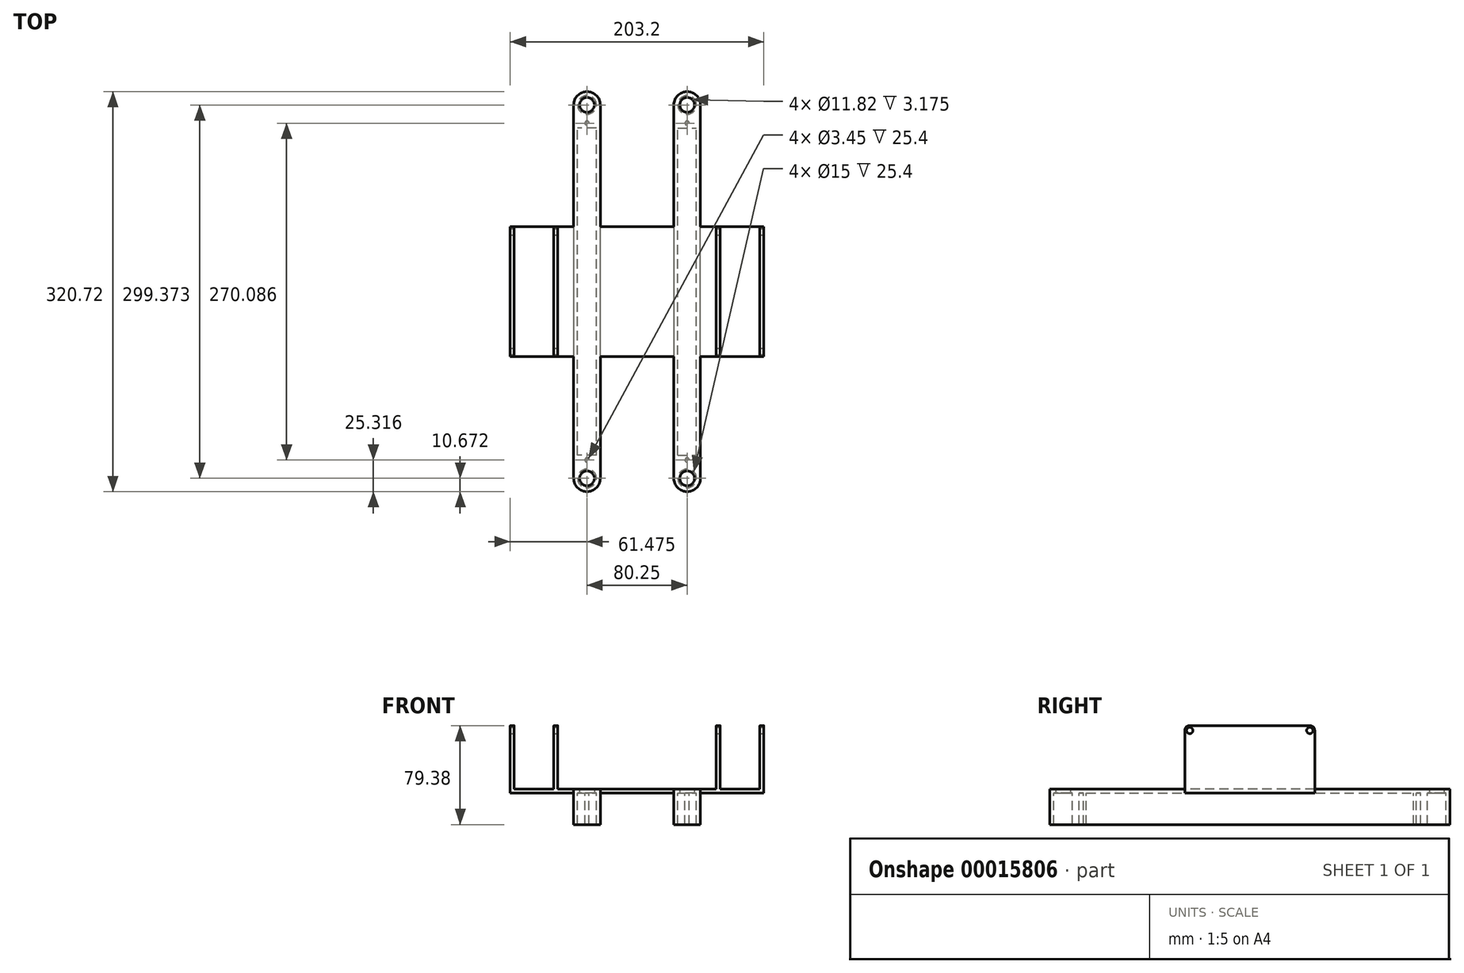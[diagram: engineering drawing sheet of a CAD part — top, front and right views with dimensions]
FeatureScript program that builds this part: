
annotation { "Feature Type Name" : "Feature", "Feature Type Description" : "" }
export const myFeature = defineFeature(function(context is Context, id is Id, definition is map)
    precondition{}
    {
        {
            var Q0;
            Q0=qCreatedBy(makeId("Top.planeOp"),FACE);
            var sketch = newSketch(context, id + "F0", { "sketchPlane" : qUnion([Q0])});
            skLineSegment(sketch, "E0.bottom", {"start": v(0, 0) * mm, "end": v(21.35, 0) * mm, "construction": true});
            skLineSegment(sketch, "E0.top", {"start": v(0, 97.64) * mm, "end": v(21.35, 97.64) * mm, "construction": true});
            skLineSegment(sketch, "E0.left", {"start": v(0, 0) * mm, "end": v(0, 97.64) * mm});
            skLineSegment(sketch, "E0.right", {"start": v(21.35, 0) * mm, "end": v(21.35, 97.64) * mm});
            skLineSegment(sketch, "E1.bottom", {"start": v(0, 0) * mm, "end": v(-50.8, 0) * mm});
            skLineSegment(sketch, "E1.top", {"start": v(0, -104.1) * mm, "end": v(-50.8, -104.1) * mm});
            skLineSegment(sketch, "E1.left", {"start": v(0, 0) * mm, "end": v(0, -104.1) * mm, "construction": true});
            skLineSegment(sketch, "E1.right", {"start": v(-50.8, 0) * mm, "end": v(-50.8, -104.1) * mm});
            skLineSegment(sketch, "E2.bottom", {"start": v(0, -104.1) * mm, "end": v(21.35, -104.1) * mm, "construction": true});
            skLineSegment(sketch, "E2.top", {"start": v(0, -201.74) * mm, "end": v(21.35, -201.74) * mm, "construction": true});
            skLineSegment(sketch, "E2.left", {"start": v(0, -104.1) * mm, "end": v(0, -201.74) * mm});
            skLineSegment(sketch, "E2.right", {"start": v(21.35, -104.1) * mm, "end": v(21.35, -201.74) * mm});
            skLineSegment(sketch, "E3.bottom", {"start": v(21.35, -104.1) * mm, "end": v(80.25, -104.1) * mm});
            skLineSegment(sketch, "E3.top", {"start": v(21.35, 0) * mm, "end": v(80.25, 0) * mm});
            skLineSegment(sketch, "E3.left", {"start": v(21.35, -104.1) * mm, "end": v(21.35, 0) * mm, "construction": true});
            skLineSegment(sketch, "E3.right", {"start": v(80.25, -104.1) * mm, "end": v(80.25, 0) * mm, "construction": true});
            skLineSegment(sketch, "E4.bottom", {"start": v(80.25, 0) * mm, "end": v(101.6, 0) * mm, "construction": true});
            skLineSegment(sketch, "E4.top", {"start": v(80.25, 97.64) * mm, "end": v(101.6, 97.64) * mm, "construction": true});
            skLineSegment(sketch, "E4.left", {"start": v(80.25, 0) * mm, "end": v(80.25, 97.64) * mm});
            skLineSegment(sketch, "E4.right", {"start": v(101.6, 0) * mm, "end": v(101.6, 97.64) * mm});
            skLineSegment(sketch, "E5.bottom", {"start": v(101.6, 0) * mm, "end": v(152.4, 0) * mm});
            skLineSegment(sketch, "E5.top", {"start": v(101.6, -104.1) * mm, "end": v(152.4, -104.1) * mm});
            skLineSegment(sketch, "E5.left", {"start": v(101.6, 0) * mm, "end": v(101.6, -104.1) * mm, "construction": true});
            skLineSegment(sketch, "E5.right", {"start": v(152.4, 0) * mm, "end": v(152.4, -104.1) * mm});
            skLineSegment(sketch, "E6.bottom", {"start": v(80.25, -104.1) * mm, "end": v(101.6, -104.1) * mm, "construction": true});
            skLineSegment(sketch, "E6.top", {"start": v(80.25, -201.74) * mm, "end": v(101.6, -201.74) * mm, "construction": true});
            skLineSegment(sketch, "E6.left", {"start": v(80.25, -104.1) * mm, "end": v(80.25, -201.74) * mm});
            skLineSegment(sketch, "E6.right", {"start": v(101.6, -104.1) * mm, "end": v(101.6, -201.74) * mm});
            skArc(sketch, "E7", {"start": v(21.35, 97.64) * mm, "mid": v(10.67, 108.31) * mm, "end": v(0, 97.64) * mm});
            skArc(sketch, "E8", {"start": v(101.6, 97.64) * mm, "mid": v(90.93, 108.31) * mm, "end": v(80.25, 97.64) * mm});
            skArc(sketch, "E9", {"start": v(80.25, -201.74) * mm, "mid": v(90.93, -212.41) * mm, "end": v(101.6, -201.74) * mm});
            skArc(sketch, "E10", {"start": v(0, -201.74) * mm, "mid": v(10.67, -212.41) * mm, "end": v(21.35, -201.74) * mm});
            skCircle(sketch, "E11", {"center": v(10.67, 97.64) * mm, "radius": 5.91 * mm});
            skCircle(sketch, "E12", {"center": v(90.93, 97.64) * mm, "radius": 5.91 * mm});
            skCircle(sketch, "E13", {"center": v(10.67, -201.74) * mm, "radius": 5.91 * mm});
            skCircle(sketch, "E14", {"center": v(90.93, -201.74) * mm, "radius": 5.91 * mm});
            skSolve(sketch);
        }
        {
            var Q0;
            Q0=qSketchRegion(id+"F0",true);
            extrude(context, id + "F1", {"entities" : qUnion([Q0]), "depth" : 3.17 * mm});
        }
        {
            var Q0;
            Q0=makeQuery(id+"F1.opExtrude","CAP_FACE",FACE,{"disambiguationData":[OSD([sQuery(id+"F0.wireOp",EDGE,"E0.left"),sQuery(id+"F0.wireOp",EDGE,"E0.right"),sQuery(id+"F0.wireOp",EDGE,"E1.bottom"),sQuery(id+"F0.wireOp",EDGE,"E1.top"),sQuery(id+"F0.wireOp",EDGE,"E1.right"),sQuery(id+"F0.wireOp",EDGE,"E2.left"),sQuery(id+"F0.wireOp",EDGE,"E2.right"),sQuery(id+"F0.wireOp",EDGE,"E3.bottom"),sQuery(id+"F0.wireOp",EDGE,"E3.top"),sQuery(id+"F0.wireOp",EDGE,"E4.left"),sQuery(id+"F0.wireOp",EDGE,"E4.right"),sQuery(id+"F0.wireOp",EDGE,"E5.bottom"),sQuery(id+"F0.wireOp",EDGE,"E5.top"),sQuery(id+"F0.wireOp",EDGE,"E5.right"),sQuery(id+"F0.wireOp",EDGE,"E6.left"),sQuery(id+"F0.wireOp",EDGE,"E6.right"),sQuery(id+"F0.wireOp",EDGE,"E7"),sQuery(id+"F0.wireOp",EDGE,"E8"),sQuery(id+"F0.wireOp",EDGE,"E9"),sQuery(id+"F0.wireOp",EDGE,"E10"),sQuery(id+"F0.wireOp",EDGE,"E11"),sQuery(id+"F0.wireOp",EDGE,"E12"),sQuery(id+"F0.wireOp",EDGE,"E13"),sQuery(id+"F0.wireOp",EDGE,"E14")])],"isStart":false});
            var sketch = newSketch(context, id + "F2", { "sketchPlane" : qUnion([Q0])});
            skLineSegment(sketch, "E15.bottom", {"start": v(-50.8, 0) * mm, "end": v(-47.63, 0) * mm});
            skLineSegment(sketch, "E15.top", {"start": v(-50.8, -104.1) * mm, "end": v(-47.62, -104.1) * mm});
            skLineSegment(sketch, "E15.left", {"start": v(-50.8, 0) * mm, "end": v(-50.8, -104.1) * mm});
            skLineSegment(sketch, "E15.right", {"start": v(-47.63, 0) * mm, "end": v(-47.63, -104.1) * mm});
            skLineSegment(sketch, "E16.bottom", {"start": v(152.4, 0) * mm, "end": v(149.22, 0) * mm});
            skLineSegment(sketch, "E16.top", {"start": v(152.4, -104.1) * mm, "end": v(149.23, -104.1) * mm});
            skLineSegment(sketch, "E16.left", {"start": v(152.4, 0) * mm, "end": v(152.4, -104.1) * mm});
            skLineSegment(sketch, "E16.right", {"start": v(149.22, 0) * mm, "end": v(149.22, -104.1) * mm});
            skLineSegment(sketch, "E17.bottom", {"start": v(-15.87, 0) * mm, "end": v(-12.7, 0) * mm});
            skLineSegment(sketch, "E17.top", {"start": v(-15.87, -104.1) * mm, "end": v(-12.7, -104.1) * mm});
            skLineSegment(sketch, "E17.left", {"start": v(-15.87, 0) * mm, "end": v(-15.87, -104.1) * mm});
            skLineSegment(sketch, "E17.right", {"start": v(-12.7, 0) * mm, "end": v(-12.7, -104.1) * mm});
            skLineSegment(sketch, "E18.bottom", {"start": v(117.48, 0) * mm, "end": v(114.3, 0) * mm});
            skLineSegment(sketch, "E18.top", {"start": v(117.48, -104.1) * mm, "end": v(114.3, -104.1) * mm});
            skLineSegment(sketch, "E18.left", {"start": v(117.48, 0) * mm, "end": v(117.48, -104.1) * mm});
            skLineSegment(sketch, "E18.right", {"start": v(114.3, 0) * mm, "end": v(114.3, -104.1) * mm});
            skLineSegment(sketch, "E19", {"start": v(117.48, -52.05) * mm, "end": v(149.22, -52.05) * mm, "construction": true});
            skLineSegment(sketch, "E20", {"start": v(-15.87, -52.05) * mm, "end": v(-47.63, -52.05) * mm, "construction": true});
            skSolve(sketch);
        }
        {
            var Q0;
            Q0 = qSketchRegion(id + "F2", true);
            extrude(context, id + "F3", {"entities" : qUnion([Q0]), "operationType" : NewBodyOperationType.ADD, "depth" : 50.8 * mm});
        }
        {
            var Q0;
            Q0=makeQuery(id+"F3.opExtrude","CAP_EDGE",EDGE,{"disambiguationData":[OSD([sQuery(id+"F2.wireOp",EDGE,"E15.bottom")])],"isStart":false});
            var Q1;
            Q1=makeQuery(id+"F3.opExtrude","CAP_EDGE",EDGE,{"disambiguationData":[OSD([sQuery(id+"F2.wireOp",EDGE,"E17.bottom")])],"isStart":false});
            var Q2;
            Q2=makeQuery(id+"F3.opExtrude","CAP_EDGE",EDGE,{"disambiguationData":[OSD([sQuery(id+"F2.wireOp",EDGE,"E17.top")])],"isStart":false});
            var Q3;
            Q3=makeQuery(id+"F3.opExtrude","CAP_EDGE",EDGE,{"disambiguationData":[OSD([sQuery(id+"F2.wireOp",EDGE,"E16.top")])],"isStart":false});
            var Q4;
            Q4=makeQuery(id+"F3.opExtrude","CAP_EDGE",EDGE,{"disambiguationData":[OSD([sQuery(id+"F2.wireOp",EDGE,"E18.top")])],"isStart":false});
            var Q5;
            Q5=makeQuery(id+"F3.opExtrude","CAP_EDGE",EDGE,{"disambiguationData":[OSD([sQuery(id+"F2.wireOp",EDGE,"E16.bottom")])],"isStart":false});
            var Q6;
            Q6=makeQuery(id+"F3.opExtrude","CAP_EDGE",EDGE,{"disambiguationData":[OSD([sQuery(id+"F2.wireOp",EDGE,"E18.bottom")])],"isStart":false});
            var Q7;
            Q7=makeQuery(id+"F3.opExtrude","CAP_EDGE",EDGE,{"disambiguationData":[OSD([sQuery(id+"F2.wireOp",EDGE,"E15.top")])],"isStart":false});
            fillet(context, id + "F4", {"entities" : qUnion([Q0, Q1, Q2, Q3, Q4, Q5, Q6, Q7]), "radius" : 3.97 * mm, "tangentPropagation" : true, "allowEdgeOverflow" : false});
        }
        {
            var Q0;
            Q0=makeQuery(id+"F3.boolean.opBoolean","MERGE",FACE,{"derivedFrom":[makeQuery(id+"F1.opExtrude","SWEPT_FACE",FACE,{"disambiguationData":[OSD([sQuery(id+"F0.wireOp",EDGE,"E5.right")])]}),makeQuery(id+"F3.opExtrude","SWEPT_FACE",FACE,{"disambiguationData":[OSD([sQuery(id+"F2.wireOp",EDGE,"E16.left")])]})]});
            var sketch = newSketch(context, id + "F5", { "sketchPlane" : qUnion([Q0])});
            skCircle(sketch, "E21", {"center": v(-100.13, 50) * mm, "radius": 2.54 * mm});
            skCircle(sketch, "E22", {"center": v(-3.97, 50) * mm, "radius": 2.54 * mm});
            skSolve(sketch);
        }
        {
            var Q0;
            Q0 = qSketchRegion(id + "F5", true);
            var Q1;
            Q1=makeQuery(id+"F3.boolean.opBoolean","MERGE",FACE,{"derivedFrom":[makeQuery(id+"F1.opExtrude","SWEPT_FACE",FACE,{"disambiguationData":[OSD([sQuery(id+"F0.wireOp",EDGE,"E1.right")])]}),makeQuery(id+"F3.opExtrude","SWEPT_FACE",FACE,{"disambiguationData":[OSD([sQuery(id+"F2.wireOp",EDGE,"E15.left")])]})]});
            extrude(context, id + "F6", {"entities" : qUnion([Q0]), "operationType" : NewBodyOperationType.REMOVE, "endBound" : BoundingType.UP_TO_SURFACE, "oppositeDirection" : true, "endBoundEntityFace" : qUnion([Q1]), "depth" : 25.4 * mm});
        }
        {
            var Q0;
            Q0=makeQuery(id+"F1.opExtrude","CAP_FACE",FACE,{"disambiguationData":[OSD([sQuery(id+"F0.wireOp",EDGE,"E0.left"),sQuery(id+"F0.wireOp",EDGE,"E0.right"),sQuery(id+"F0.wireOp",EDGE,"E1.bottom"),sQuery(id+"F0.wireOp",EDGE,"E1.top"),sQuery(id+"F0.wireOp",EDGE,"E1.right"),sQuery(id+"F0.wireOp",EDGE,"E2.left"),sQuery(id+"F0.wireOp",EDGE,"E2.right"),sQuery(id+"F0.wireOp",EDGE,"E3.bottom"),sQuery(id+"F0.wireOp",EDGE,"E3.top"),sQuery(id+"F0.wireOp",EDGE,"E4.left"),sQuery(id+"F0.wireOp",EDGE,"E4.right"),sQuery(id+"F0.wireOp",EDGE,"E5.bottom"),sQuery(id+"F0.wireOp",EDGE,"E5.top"),sQuery(id+"F0.wireOp",EDGE,"E5.right"),sQuery(id+"F0.wireOp",EDGE,"E6.left"),sQuery(id+"F0.wireOp",EDGE,"E6.right"),sQuery(id+"F0.wireOp",EDGE,"E7"),sQuery(id+"F0.wireOp",EDGE,"E8"),sQuery(id+"F0.wireOp",EDGE,"E9"),sQuery(id+"F0.wireOp",EDGE,"E10"),sQuery(id+"F0.wireOp",EDGE,"E11"),sQuery(id+"F0.wireOp",EDGE,"E12"),sQuery(id+"F0.wireOp",EDGE,"E13"),sQuery(id+"F0.wireOp",EDGE,"E14")])],"isStart":true});
            var sketch = newSketch(context, id + "F7", { "sketchPlane" : qUnion([Q0])});
            skCircle(sketch, "E23", {"center": v(90.93, -97.64) * mm, "radius": 7.5 * mm});
            skCircle(sketch, "E24", {"center": v(10.67, -97.64) * mm, "radius": 7.5 * mm});
            skCircle(sketch, "E25", {"center": v(10.67, 201.74) * mm, "radius": 7.5 * mm});
            skCircle(sketch, "E26", {"center": v(90.93, 201.74) * mm, "radius": 7.5 * mm});
            skArc(sketch, "E27", {"start": v(80.25, -97.64) * mm, "mid": v(90.93, -108.31) * mm, "end": v(101.6, -97.64) * mm});
            skArc(sketch, "E28", {"start": v(0, -97.64) * mm, "mid": v(10.67, -108.31) * mm, "end": v(21.35, -97.64) * mm});
            skArc(sketch, "E29", {"start": v(21.35, 201.74) * mm, "mid": v(10.67, 212.41) * mm, "end": v(0, 201.74) * mm});
            skArc(sketch, "E30", {"start": v(101.6, 201.74) * mm, "mid": v(90.93, 212.41) * mm, "end": v(80.25, 201.74) * mm});
            skArc(sketch, "E31", {"start": v(80.25, 201.74) * mm, "mid": v(90.93, 191.06) * mm, "end": v(101.6, 201.74) * mm, "construction": true});
            skCircle(sketch, "E32", {"center": v(90.93, 187.1) * mm, "radius": 3.97 * mm, "construction": true});
            skLineSegment(sketch, "E33", {"start": v(90.93, 201.74) * mm, "end": v(90.93, 187.1) * mm, "construction": true});
            skLineSegment(sketch, "E34", {"start": v(10.67, 201.74) * mm, "end": v(10.67, 187.1) * mm, "construction": true});
            skLineSegment(sketch, "E35", {"start": v(90.93, -97.64) * mm, "end": v(90.93, -83) * mm, "construction": true});
            skLineSegment(sketch, "E36", {"start": v(10.67, -97.64) * mm, "end": v(10.67, -83) * mm, "construction": true});
            skCircle(sketch, "E37", {"center": v(10.67, 187.1) * mm, "radius": 1.73 * mm});
            skCircle(sketch, "E38", {"center": v(90.93, 187.1) * mm, "radius": 1.73 * mm});
            skCircle(sketch, "E39", {"center": v(90.93, -83) * mm, "radius": 1.73 * mm});
            skCircle(sketch, "E40", {"center": v(10.67, -83) * mm, "radius": 1.73 * mm});
            skLineSegment(sketch, "E41.bottom", {"start": v(101.6, 201.74) * mm, "end": v(80.25, 201.74) * mm});
            skLineSegment(sketch, "E41.top", {"start": v(101.6, -97.64) * mm, "end": v(80.25, -97.64) * mm});
            skLineSegment(sketch, "E41.left", {"start": v(101.6, 201.74) * mm, "end": v(101.6, -97.64) * mm});
            skLineSegment(sketch, "E41.right", {"start": v(80.25, 201.74) * mm, "end": v(80.25, -97.64) * mm});
            skLineSegment(sketch, "E42.bottom", {"start": v(21.35, -97.64) * mm, "end": v(0, -97.64) * mm});
            skLineSegment(sketch, "E42.top", {"start": v(21.35, 201.74) * mm, "end": v(0, 201.74) * mm});
            skLineSegment(sketch, "E42.left", {"start": v(21.35, -97.64) * mm, "end": v(21.35, 201.74) * mm});
            skLineSegment(sketch, "E42.right", {"start": v(0, -97.64) * mm, "end": v(0, 201.74) * mm});
            skLineSegment(sketch, "E43", {"start": v(21.35, 52.05) * mm, "end": v(0, 52.05) * mm, "construction": true});
            skLineSegment(sketch, "E44", {"start": v(101.6, 52.05) * mm, "end": v(80.25, 52.05) * mm, "construction": true});
            skLineSegment(sketch, "E45.rect.bottom", {"start": v(83.43, 183.13) * mm, "end": v(98.43, 183.13) * mm});
            skLineSegment(sketch, "E45.rect.top", {"start": v(83.43, -79.02) * mm, "end": v(98.43, -79.02) * mm});
            skLineSegment(sketch, "E45.rect.left", {"start": v(83.43, 183.13) * mm, "end": v(83.43, -79.02) * mm});
            skLineSegment(sketch, "E45.rect.right", {"start": v(98.43, 183.13) * mm, "end": v(98.43, -79.02) * mm});
            skPoint(sketch, "E45.rect.middle", {"position": v(90.93, 52.05) * mm});
            skLineSegment(sketch, "E46.rect.bottom", {"start": v(18.17, 183.13) * mm, "end": v(3.17, 183.13) * mm});
            skLineSegment(sketch, "E46.rect.top", {"start": v(18.17, -79.02) * mm, "end": v(3.17, -79.02) * mm});
            skLineSegment(sketch, "E46.rect.left", {"start": v(18.17, 183.13) * mm, "end": v(18.17, -79.02) * mm});
            skLineSegment(sketch, "E46.rect.right", {"start": v(3.17, 183.13) * mm, "end": v(3.17, -79.02) * mm});
            skPoint(sketch, "E46.rect.middle", {"position": v(10.67, 52.05) * mm});
            skSolve(sketch);
        }
        {
            var Q0;
            Q0 = qSketchRegion(id + "F7", true);
            extrude(context, id + "F8", {"entities" : qUnion([Q0]), "operationType" : NewBodyOperationType.ADD, "depth" : 25.4 * mm});
        }
    });
